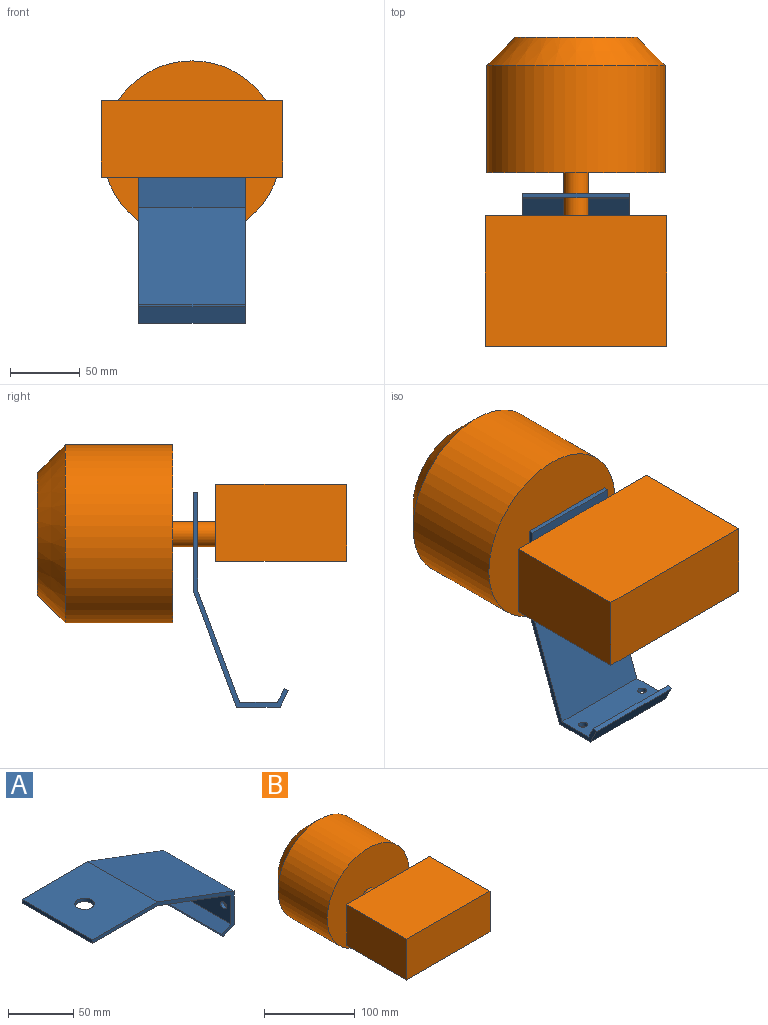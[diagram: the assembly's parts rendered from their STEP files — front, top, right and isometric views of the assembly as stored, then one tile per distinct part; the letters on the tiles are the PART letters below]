
ASSEMBLY  parts=2 mates=1
PART A: 15 faces, bbox 154.3x76.2x68.3 mm
  f0: plane 76.15x3.3mm, normal (-1,0,0), area 251.3mm2, adj f1,f9,f10,f11
  f1: plane 76.15x71mm, normal (0,0,-1), area 5229.9mm2, adj f0,f2,f10,f11,f12
  f2: plane 80x76.15mm, normal (-0.35,0,-0.94), area 6506.3mm2, adj f1,f3,f10,f11
  f3: plane 76.15x27mm, normal (-1,0,0), area 1994.7mm2, adj f2,f4,f10,f11,f13,f14
  f4: plane 76.15x10mm, normal (-0.45,0,0.89), area 851.4mm2, adj f3,f5,f10,f11
  f5: plane 76.15x2.95mm, normal (-0.89,0,-0.45), area 251.3mm2, adj f4,f6,f10,f11
  f6: plane 76.15x11.82mm, normal (0.45,0,-0.89), area 1006.7mm2, adj f5,f7,f10,f11
  f7: plane 76.15x31.33mm, normal (1,0,0), area 2324.1mm2, adj f6,f8,f10,f11,f13,f14
  f8: plane 82.7x76.15mm, normal (0.35,0,0.94), area 6726mm2, adj f7,f9,f10,f11
  f9: plane 76.15x71.6mm, normal (0,0,1), area 5275.5mm2, adj f0,f8,f10,f11,f12
  f10: plane 154.3x68.25mm, normal (0,-1,0), area 658.5mm2, adj f0,f1,f2,f3,f4,f5,f6,f7
  f11: plane 154.3x68.25mm, normal (0,1,0), area 658.5mm2, adj f0,f1,f2,f3,f4,f5,f6,f7
  f12: cylinder r=7.5mm len=15mm, axis (0,0,1), area 155.5mm2, adj f1,f9
  f13: cylinder r=3.12mm len=6.25mm, axis (1,0,0), area 64.8mm2, adj f3,f7
  f14: cylinder r=3.12mm len=6.25mm, axis (1,0,0), area 64.8mm2, adj f3,f7
PART B: 11 faces, bbox 130x222x128 mm
  f0: plane 94x55.2mm, normal (-1,0,0), area 5188.8mm2, adj f1,f3,f4,f5
  f1: plane 130x55.2mm, normal (0,-1,0), area 7176mm2, adj f0,f2,f4,f5
  f2: plane 94x55.2mm, normal (1,0,0), area 5188.8mm2, adj f1,f3,f4,f5
  f3: plane 130x55.2mm, normal (0,1,0), area 6921.5mm2, adj f0,f2,f4,f5,f6
  f4: plane 130x94mm, normal (0,0,1), area 12220mm2, adj f0,f1,f2,f3
  f5: plane 130x94mm, normal (0,0,-1), area 12220mm2, adj f0,f1,f2,f3
  f6: cylinder r=9mm len=31mm, axis (0,-1,0), area 1753mm2, adj f3,f9
  f7: cylinder r=64mm len=128mm, axis (0,-1,0), area 30963.5mm2, adj f9,f10
  f8: plane 88x88mm, normal (0,1,0), area 6082.1mm2, adj f10
  f9: plane 128x128mm, normal (0,-1,0), area 12613.5mm2, adj f6,f7
  f10: cone r=44mm half-angle=45deg, axis (0,-1,0), area 9596.6mm2, adj f7,f8
PLACE A rot(axis=(-0.58,0.58,0.58),120deg) t=(-167.39,-89.83,13.69)mm
PLACE B t=(-194.32,-196.53,-35.81)mm
MATE fastened A.f12 <-> B.f6  axis (0,1,0) through (-129.32,-86.53,-16.31)mm
